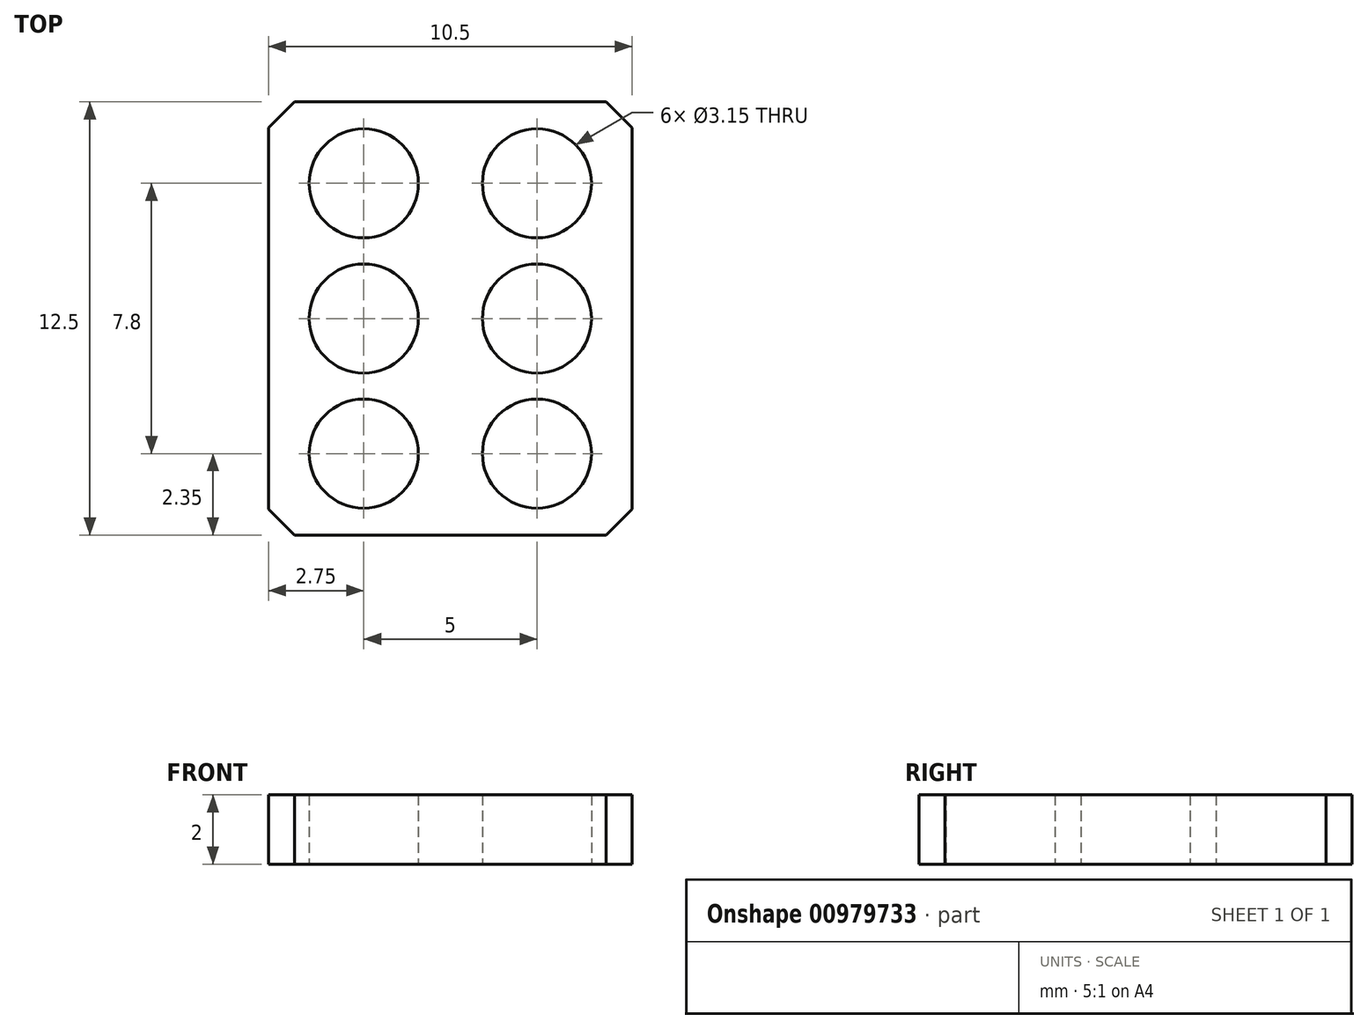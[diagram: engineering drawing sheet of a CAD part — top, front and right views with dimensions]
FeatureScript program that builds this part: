
annotation { "Feature Type Name" : "Feature", "Feature Type Description" : "" }
export const myFeature = defineFeature(function(context is Context, id is Id, definition is map)
    precondition{}
    {
        {
            var Q0;
            Q0=qCreatedBy(makeId("Top.planeOp"),FACE);
            var sketch = newSketch(context, id + "F0", { "sketchPlane" : qUnion([Q0])});
            skLineSegment(sketch, "E0.bottom", {"start": v(5.25, 6.25) * mm, "end": v(-5.25, 6.25) * mm});
            skLineSegment(sketch, "E0.top", {"start": v(5.25, -6.25) * mm, "end": v(-5.25, -6.25) * mm});
            skLineSegment(sketch, "E0.left", {"start": v(5.25, 6.25) * mm, "end": v(5.25, -6.25) * mm});
            skLineSegment(sketch, "E0.right", {"start": v(-5.25, 6.25) * mm, "end": v(-5.25, -6.25) * mm});
            skPoint(sketch, "E0.middle", {"position": v(0, 0) * mm});
            skCircle(sketch, "E1", {"center": v(-2.5, 3.9) * mm, "radius": 1.57 * mm});
            skCircle(sketch, "E2", {"center": v(2.5, 3.9) * mm, "radius": 1.57 * mm});
            skCircle(sketch, "E3", {"center": v(2.5, 0) * mm, "radius": 1.57 * mm});
            skCircle(sketch, "E4", {"center": v(2.5, -3.9) * mm, "radius": 1.57 * mm});
            skCircle(sketch, "E5", {"center": v(-2.5, -3.9) * mm, "radius": 1.57 * mm});
            skCircle(sketch, "E6", {"center": v(-2.5, 0) * mm, "radius": 1.57 * mm});
            skSolve(sketch);
        }
        {
            var Q0;
            Q0 = qSketchRegion(id + "F0", true);
            extrude(context, id + "F1", {"entities" : qUnion([Q0]), "depth" : 2 * mm, "offsetDistance" : 25 * mm});
        }
        {
            var Q0;
            Q0=makeQuery(id+"F1.opExtrude","SWEPT_EDGE",EDGE,{"disambiguationData":[OSD([sQuery(id+"F0.wireOp",EDGE,"E0.bottom"),sQuery(id+"F0.wireOp",EDGE,"E0.right")])]});
            var Q1;
            Q1=makeQuery(id+"F1.opExtrude","SWEPT_EDGE",EDGE,{"disambiguationData":[OSD([sQuery(id+"F0.wireOp",EDGE,"E0.bottom"),sQuery(id+"F0.wireOp",EDGE,"E0.left")])]});
            var Q2;
            Q2=makeQuery(id+"F1.opExtrude","SWEPT_EDGE",EDGE,{"disambiguationData":[OSD([sQuery(id+"F0.wireOp",EDGE,"E0.top"),sQuery(id+"F0.wireOp",EDGE,"E0.left")])]});
            var Q3;
            Q3=makeQuery(id+"F1.opExtrude","SWEPT_EDGE",EDGE,{"disambiguationData":[OSD([sQuery(id+"F0.wireOp",EDGE,"E0.top"),sQuery(id+"F0.wireOp",EDGE,"E0.right")])]});
            chamfer(context, id + "F2", {"entities" : qUnion([Q0, Q1, Q2, Q3]), "width" : 0.75 * mm, "tangentPropagation" : true});
        }
    });
